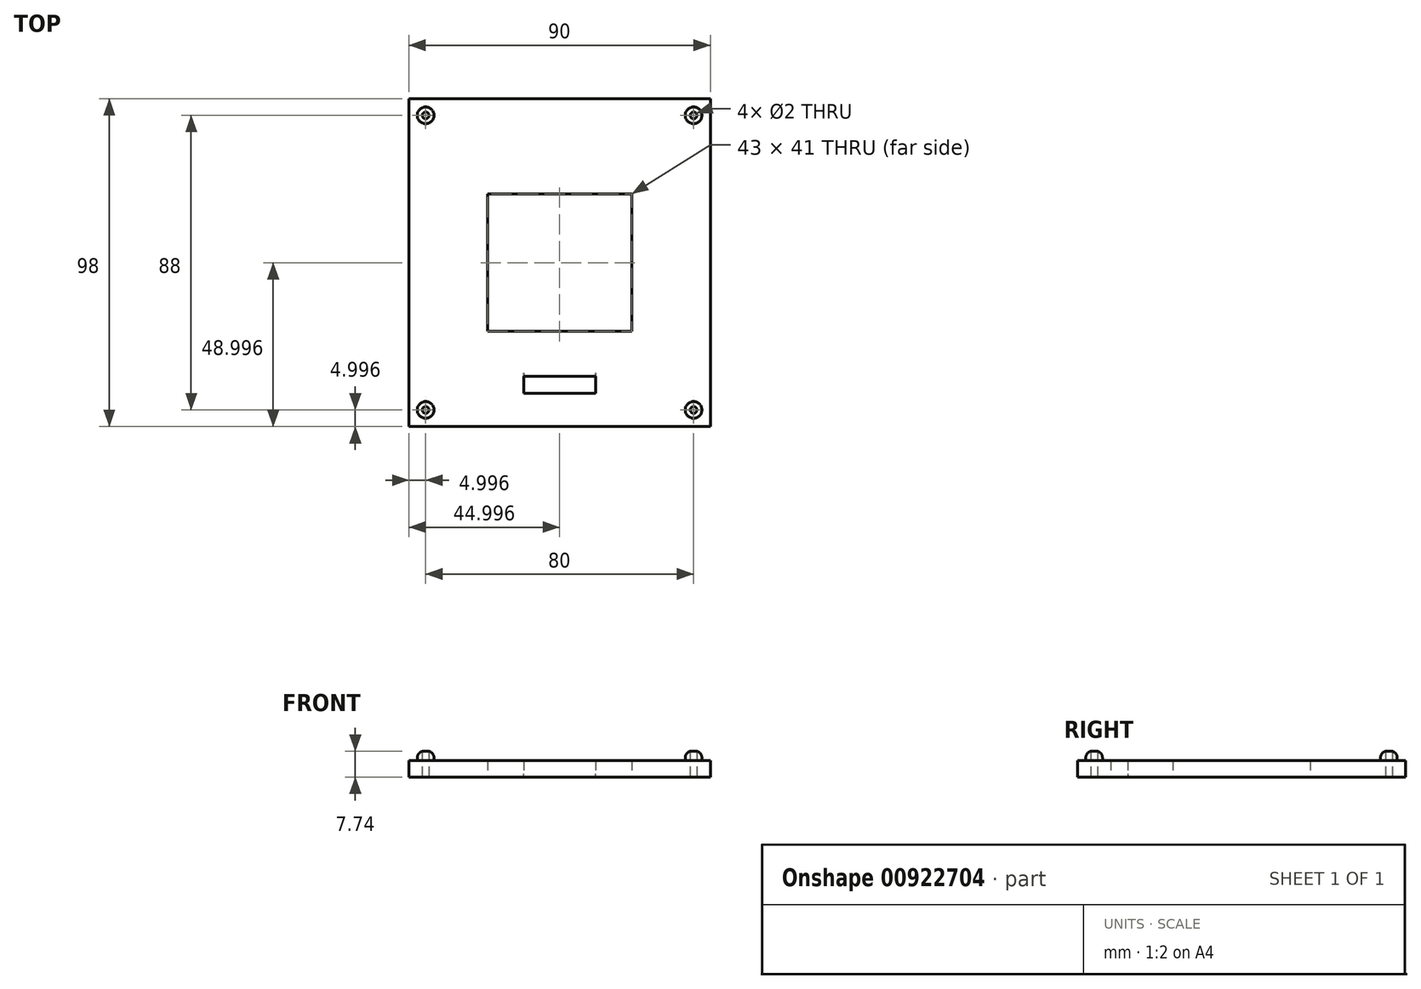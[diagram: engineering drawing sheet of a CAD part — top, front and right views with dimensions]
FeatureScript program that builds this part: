
annotation { "Feature Type Name" : "Feature", "Feature Type Description" : "" }
export const myFeature = defineFeature(function(context is Context, id is Id, definition is map)
    precondition{}
    {
        {
            var Q0;
            Q0=qCreatedBy(makeId("Top.planeOp"),FACE);
            var sketch = newSketch(context, id + "F0", { "sketchPlane" : qUnion([Q0])});
            skLineSegment(sketch, "E0.bottom", {"start": v(-26.62, 40.09) * mm, "end": v(43.38, 40.09) * mm});
            skLineSegment(sketch, "E0.top", {"start": v(-26.62, -37.91) * mm, "end": v(43.38, -37.91) * mm});
            skLineSegment(sketch, "E0.left", {"start": v(-26.62, 40.09) * mm, "end": v(-26.62, -37.91) * mm});
            skLineSegment(sketch, "E0.right", {"start": v(43.38, 40.09) * mm, "end": v(43.38, -37.91) * mm});
            skLineSegment(sketch, "E1.bottom", {"start": v(-36.62, 50.09) * mm, "end": v(53.38, 50.09) * mm});
            skLineSegment(sketch, "E1.top", {"start": v(-36.62, -47.91) * mm, "end": v(53.38, -47.91) * mm});
            skLineSegment(sketch, "E1.left", {"start": v(-36.62, 50.09) * mm, "end": v(-36.62, -47.91) * mm});
            skLineSegment(sketch, "E1.right", {"start": v(53.38, 50.09) * mm, "end": v(53.38, -47.91) * mm});
            skLineSegment(sketch, "E2", {"start": v(0, -47.91) * mm, "end": v(0, -37.91) * mm, "construction": true});
            skLineSegment(sketch, "E3", {"start": v(-36.62, 0) * mm, "end": v(-26.62, 0) * mm, "construction": true});
            skLineSegment(sketch, "E4", {"start": v(8.38, 40.09) * mm, "end": v(8.38, -37.91) * mm, "construction": true});
            skLineSegment(sketch, "E5", {"start": v(-2.37, -37.91) * mm, "end": v(-2.37, -32.91) * mm});
            skLineSegment(sketch, "E6", {"start": v(19.13, -37.91) * mm, "end": v(19.13, -32.91) * mm});
            skLineSegment(sketch, "E7", {"start": v(19.13, -32.91) * mm, "end": v(-2.37, -32.91) * mm});
            skLineSegment(sketch, "E8.bottom", {"start": v(-31.62, 45.09) * mm, "end": v(48.38, 45.09) * mm});
            skLineSegment(sketch, "E8.top", {"start": v(-31.62, -42.91) * mm, "end": v(48.38, -42.91) * mm});
            skLineSegment(sketch, "E8.left", {"start": v(-31.62, 45.09) * mm, "end": v(-31.62, -42.91) * mm});
            skLineSegment(sketch, "E8.right", {"start": v(48.38, 45.09) * mm, "end": v(48.38, -42.91) * mm});
            skCircle(sketch, "E9", {"center": v(-31.62, 45.09) * mm, "radius": 2.5 * mm});
            skCircle(sketch, "E10", {"center": v(48.38, 45.09) * mm, "radius": 2.5 * mm});
            skCircle(sketch, "E11", {"center": v(48.38, -42.91) * mm, "radius": 2.5 * mm});
            skCircle(sketch, "E12", {"center": v(-31.62, -42.91) * mm, "radius": 2.5 * mm});
            skLineSegment(sketch, "E13", {"start": v(43.38, 1.09) * mm, "end": v(-26.62, 1.09) * mm, "construction": true});
            skLineSegment(sketch, "E14.bottom", {"start": v(29.88, -19.41) * mm, "end": v(-13.12, -19.41) * mm});
            skLineSegment(sketch, "E14.top", {"start": v(29.88, 21.59) * mm, "end": v(-13.12, 21.59) * mm});
            skLineSegment(sketch, "E14.left", {"start": v(29.88, -19.41) * mm, "end": v(29.88, 21.59) * mm});
            skLineSegment(sketch, "E14.right", {"start": v(-13.12, -19.41) * mm, "end": v(-13.12, 21.59) * mm});
            skPoint(sketch, "E14.middle", {"position": v(8.38, 1.09) * mm});
            skLineSegment(sketch, "E15", {"start": v(29.88, -15.19) * mm, "end": v(25.4, -19.41) * mm});
            skLineSegment(sketch, "E16", {"start": v(-8.99, -19.41) * mm, "end": v(-13.12, -15.04) * mm});
            skLineSegment(sketch, "E17", {"start": v(-13.12, 18.16) * mm, "end": v(-9.5, 21.59) * mm});
            skLineSegment(sketch, "E18", {"start": v(29.88, 17.34) * mm, "end": v(25.8, 21.59) * mm});
            skSolve(sketch);
        }
        {
            var Q0;
            Q0=makeQuery(id+"F0.imprint","IMPRINT",FACE,{"disambiguationData":[TD([[makeQuery(id+"F0.imprint","IMPRINT",EDGE,{"derivedFrom":sQuery(id+"F0.wireOp",EDGE,"E0.bottom")}),-1.0]])]});
            extrude(context, id + "F1", {"entities" : qUnion([Q0]), "depth" : 5 * mm, "offsetDistance" : 25 * mm});
        }
        {
            var Q0;
            Q0=makeQuery(id+"F0.imprint","IMPRINT",FACE,{"disambiguationData":[TD([[makeQuery(id+"F0.imprint","IMPRINT",EDGE,{"derivedFrom":sQuery(id+"F0.wireOp",EDGE,"E0.bottom")}),1.0]])]});
            var Q1;
            Q1=makeQuery(id+"F0.imprint","IMPRINT",FACE,{"disambiguationData":[TD([[makeQuery(id+"F0.imprint","IMPRINT",EDGE,{"derivedFrom":sQuery(id+"F0.wireOp",EDGE,"E1.bottom")}),-1.0]])]});
            extrude(context, id + "F2", {"entities" : qUnion([Q0, Q1]), "operationType" : NewBodyOperationType.ADD, "depth" : 5 * mm, "offsetDistance" : 25 * mm});
        }
        {
            var Q0;
            {var subQ0=sQuery(id+"F0.wireOp",EDGE,"E8.left");var subQ1=sQuery(id+"F0.wireOp",EDGE,"E8.bottom");var subQ2=makeQuery(id+"F0.imprint","INTERSECT",VERTEX,{"derivedFrom":[subQ1,subQ0]});Q0=makeQuery(id+"F0.imprint","IMPRINT",FACE,{"disambiguationData":[TD([[makeQuery(id+"F0.imprint","IMPRINT",EDGE,{"disambiguationData":[TD([[subQ2,-1.0]])],"derivedFrom":subQ1}),1.0]])]});}
            var Q1;
            {var subQ0=sQuery(id+"F0.wireOp",EDGE,"E8.left");var subQ1=sQuery(id+"F0.wireOp",EDGE,"E8.bottom");var subQ2=makeQuery(id+"F0.imprint","INTERSECT",VERTEX,{"derivedFrom":[subQ1,subQ0]});Q1=makeQuery(id+"F0.imprint","IMPRINT",FACE,{"disambiguationData":[TD([[makeQuery(id+"F0.imprint","IMPRINT",EDGE,{"disambiguationData":[TD([[subQ2,-1.0]])],"derivedFrom":subQ1}),-1.0]])]});}
            var Q2;
            {var subQ0=sQuery(id+"F0.wireOp",EDGE,"E8.right");var subQ1=sQuery(id+"F0.wireOp",EDGE,"E8.bottom");var subQ2=makeQuery(id+"F0.imprint","INTERSECT",VERTEX,{"derivedFrom":[subQ1,subQ0]});Q2=makeQuery(id+"F0.imprint","IMPRINT",FACE,{"disambiguationData":[TD([[makeQuery(id+"F0.imprint","IMPRINT",EDGE,{"disambiguationData":[TD([[subQ2,1.0]])],"derivedFrom":subQ1}),-1.0]])]});}
            var Q3;
            {var subQ0=sQuery(id+"F0.wireOp",EDGE,"E8.right");var subQ1=sQuery(id+"F0.wireOp",EDGE,"E8.bottom");var subQ2=makeQuery(id+"F0.imprint","INTERSECT",VERTEX,{"derivedFrom":[subQ1,subQ0]});Q3=makeQuery(id+"F0.imprint","IMPRINT",FACE,{"disambiguationData":[TD([[makeQuery(id+"F0.imprint","IMPRINT",EDGE,{"disambiguationData":[TD([[subQ2,1.0]])],"derivedFrom":subQ1}),1.0]])]});}
            var Q4;
            {var subQ0=sQuery(id+"F0.wireOp",EDGE,"E8.right");var subQ1=sQuery(id+"F0.wireOp",EDGE,"E8.top");var subQ2=makeQuery(id+"F0.imprint","INTERSECT",VERTEX,{"derivedFrom":[subQ1,subQ0]});Q4=makeQuery(id+"F0.imprint","IMPRINT",FACE,{"disambiguationData":[TD([[makeQuery(id+"F0.imprint","IMPRINT",EDGE,{"disambiguationData":[TD([[subQ2,1.0]])],"derivedFrom":subQ1}),-1.0]])]});}
            var Q5;
            {var subQ0=sQuery(id+"F0.wireOp",EDGE,"E8.right");var subQ1=sQuery(id+"F0.wireOp",EDGE,"E8.top");var subQ2=makeQuery(id+"F0.imprint","INTERSECT",VERTEX,{"derivedFrom":[subQ1,subQ0]});Q5=makeQuery(id+"F0.imprint","IMPRINT",FACE,{"disambiguationData":[TD([[makeQuery(id+"F0.imprint","IMPRINT",EDGE,{"disambiguationData":[TD([[subQ2,1.0]])],"derivedFrom":subQ1}),1.0]])]});}
            var Q6;
            {var subQ0=sQuery(id+"F0.wireOp",EDGE,"E8.left");var subQ1=sQuery(id+"F0.wireOp",EDGE,"E8.top");var subQ2=makeQuery(id+"F0.imprint","INTERSECT",VERTEX,{"derivedFrom":[subQ1,subQ0]});Q6=makeQuery(id+"F0.imprint","IMPRINT",FACE,{"disambiguationData":[TD([[makeQuery(id+"F0.imprint","IMPRINT",EDGE,{"disambiguationData":[TD([[subQ2,-1.0]])],"derivedFrom":subQ1}),-1.0]])]});}
            var Q7;
            {var subQ0=sQuery(id+"F0.wireOp",EDGE,"E8.left");var subQ1=sQuery(id+"F0.wireOp",EDGE,"E8.top");var subQ2=makeQuery(id+"F0.imprint","INTERSECT",VERTEX,{"derivedFrom":[subQ1,subQ0]});Q7=makeQuery(id+"F0.imprint","IMPRINT",FACE,{"disambiguationData":[TD([[makeQuery(id+"F0.imprint","IMPRINT",EDGE,{"disambiguationData":[TD([[subQ2,-1.0]])],"derivedFrom":subQ1}),1.0]])]});}
            var Q8;
            Q8=sQuery(id+"F0.wireOp",EDGE,"E9");
            var Q9;
            Q9=sQuery(id+"F0.wireOp",EDGE,"E10");
            var Q10;
            Q10=sQuery(id+"F0.wireOp",EDGE,"E11");
            var Q11;
            Q11=sQuery(id+"F0.wireOp",EDGE,"E12");
            extrude(context, id + "F3", {"entities" : qUnion([Q0, Q1, Q2, Q3, Q4, Q5, Q6, Q7]), "operationType" : NewBodyOperationType.ADD, "surfaceEntities" : qUnion([Q8, Q9, Q10, Q11]), "depth" : 7.8 * mm, "offsetDistance" : 25 * mm});
        }
        {
            var Q0;
            Q0=makeQuery(id+"F3.opExtrude","CAP_EDGE",EDGE,{"disambiguationData":[OSD([sQuery(id+"F0.wireOp",EDGE,"E9")])],"isStart":false});
            var Q1;
            Q1=makeQuery(id+"F3.opExtrude","CAP_EDGE",EDGE,{"disambiguationData":[OSD([sQuery(id+"F0.wireOp",EDGE,"E12")])],"isStart":false});
            var Q2;
            Q2=makeQuery(id+"F3.opExtrude","CAP_EDGE",EDGE,{"disambiguationData":[OSD([sQuery(id+"F0.wireOp",EDGE,"E11")])],"isStart":false});
            var Q3;
            Q3=makeQuery(id+"F3.opExtrude","CAP_EDGE",EDGE,{"disambiguationData":[OSD([sQuery(id+"F0.wireOp",EDGE,"E10")])],"isStart":false});
            fillet(context, id + "F4", {"entities" : qUnion([Q0, Q1, Q2, Q3]), "radius" : 2 * mm, "tangentPropagation" : true, "allowEdgeOverflow" : false});
        }
        {
            var Q0;
            Q0=sQuery(id+"F0.wireOp",VERTEX,"E8.bottom.end");
            var Q1;
            Q1=sQuery(id+"F0.wireOp",VERTEX,"E8.top.end");
            var Q2;
            Q2=sQuery(id+"F0.wireOp",VERTEX,"E8.top.start");
            var Q3;
            Q3=sQuery(id+"F0.wireOp",VERTEX,"E8.bottom.start");
            var Q4;
            Q4=makeQuery(id+"F1.opExtrude","SWEPT_BODY",BODY,{"disambiguationData":[OSD([sQuery(id+"F0.wireOp",EDGE,"E0.bottom"),sQuery(id+"F0.wireOp",EDGE,"E0.top"),sQuery(id+"F0.wireOp",EDGE,"E0.left"),sQuery(id+"F0.wireOp",EDGE,"E0.right"),sQuery(id+"F0.wireOp",EDGE,"E5"),sQuery(id+"F0.wireOp",EDGE,"E6"),sQuery(id+"F0.wireOp",EDGE,"E7")])]});
            hole(context, id + "F5", {"style" : HoleStyle.SIMPLE, "endStyle" : HoleEndStyle.THROUGH, "oppositeDirection" : true, "holeDiameter" : 2 * mm, "majorDiameter" : 5 * mm, "isTappedThrough" : true, "tappedDepth" : 12 * mm, "tapClearance" : 3, "locations" : qUnion([Q0, Q1, Q2, Q3]), "scope" : qUnion([Q4])});
        }
        {
            var Q0;
            Q0=makeQuery(id+"F1.opExtrude","CAP_EDGE",EDGE,{"disambiguationData":[OSD([sQuery(id+"F0.wireOp",EDGE,"E7")])],"isStart":true});
            fillet(context, id + "F6", {"entities" : qUnion([Q0]), "radius" : 1 * mm, "tangentPropagation" : true, "allowEdgeOverflow" : false});
        }
    });
